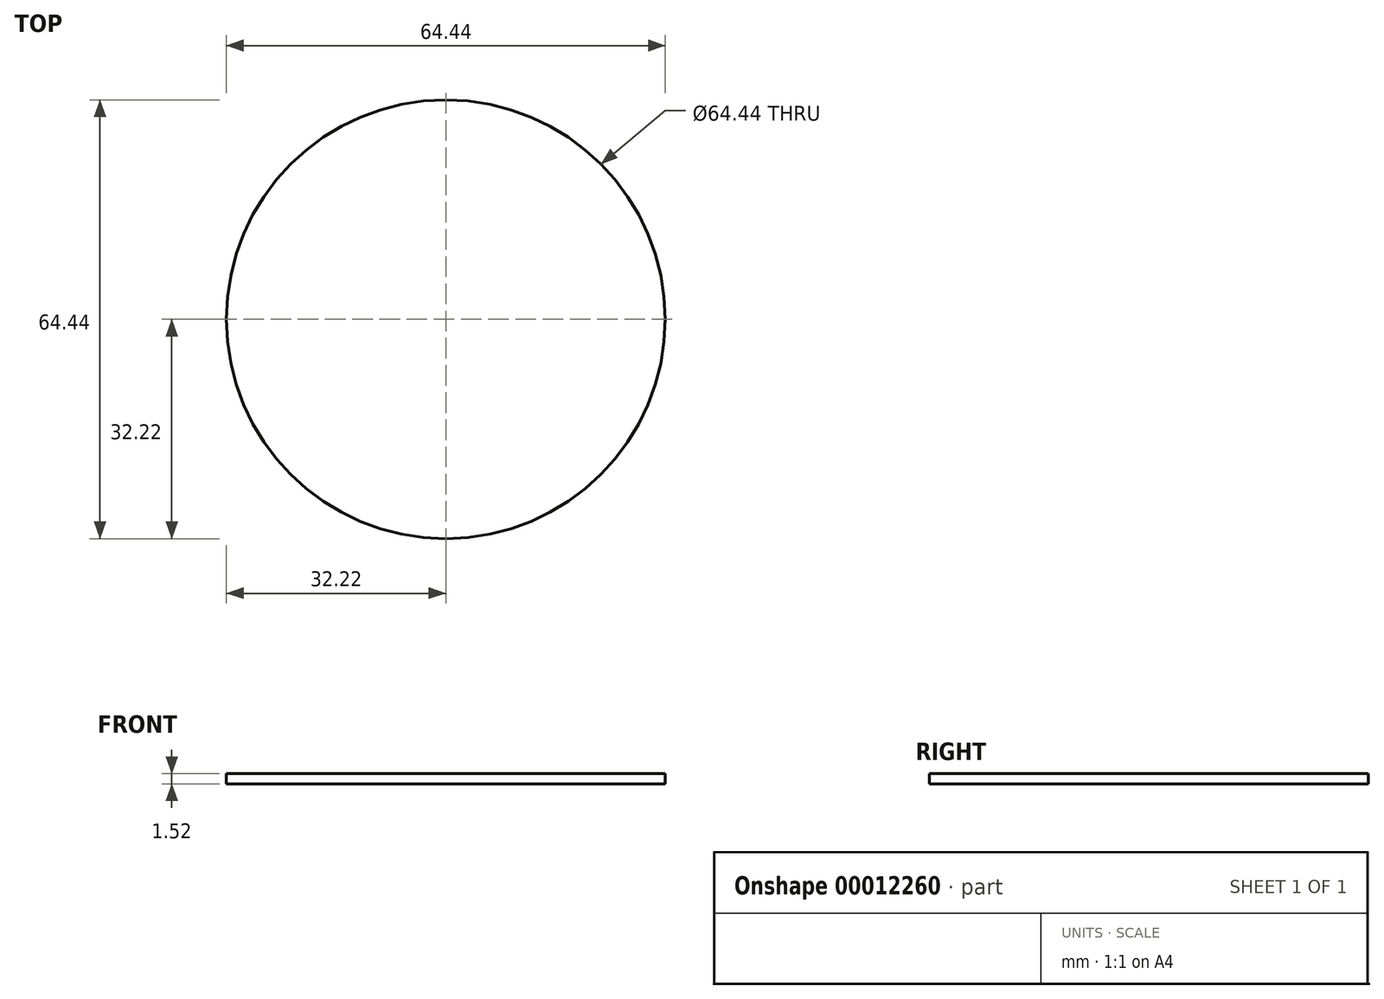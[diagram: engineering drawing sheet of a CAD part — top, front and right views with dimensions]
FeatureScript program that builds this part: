
annotation { "Feature Type Name" : "Feature", "Feature Type Description" : "" }
export const myFeature = defineFeature(function(context is Context, id is Id, definition is map)
    precondition{}
    {
        {
            var Q0;
            Q0=qCreatedBy(makeId("Top.planeOp"),FACE);
            var sketch = newSketch(context, id + "F0", { "sketchPlane" : qUnion([Q0])});
            skCircle(sketch, "E0", {"center": v(0, 0) * mm, "radius": 32.22 * mm});
            skSolve(sketch);
        }
        {
            var Q0;
            Q0=makeQuery(id+"F0.imprint","IMPRINT",FACE,{"disambiguationData":[TD([[makeQuery(id+"F0.imprint","IMPRINT",EDGE,{"derivedFrom":sQuery(id+"F0.wireOp",EDGE,"E0")}),1.0]])]});
            var sketch = newSketch(context, id + "F1", { "sketchPlane" : qUnion([Q0])});
            skSolve(sketch);
        }
        {
            var Q0;
            Q0=makeQuery(id+"F0.imprint","IMPRINT",FACE,{"disambiguationData":[TD([[makeQuery(id+"F0.imprint","IMPRINT",EDGE,{"derivedFrom":sQuery(id+"F0.wireOp",EDGE,"E0")}),1.0]])]});
            var Q1;
            Q1=makeQuery(id+"F1.imprint","IMPRINT",FACE,{"disambiguationData":[TD([[makeQuery(id+"F1.imprint","IMPRINT",EDGE,{"derivedFrom":makeQuery(id+"F0.imprint","IMPRINT",EDGE,{"derivedFrom":sQuery(id+"F0.wireOp",EDGE,"E0")})}),1.0]])]});
            var Q2;
            Q2 = qConstructionFilter(qBodyType(qCreatedBy(id + "F0" ,EDGE), BodyType.WIRE), ConstructionObject.NO);
            var Q3;
            Q3 = qConstructionFilter(qBodyType(qCreatedBy(id + "F1" ,EDGE), BodyType.WIRE), ConstructionObject.NO);
            extrude(context, id + "F2", {"entities" : qUnion([Q0, Q1]), "bodyType" : ToolBodyType.SURFACE, "surfaceEntities" : qUnion([Q2, Q3]), "oppositeDirection" : true, "depth" : 1.52 * mm});
        }
    });
